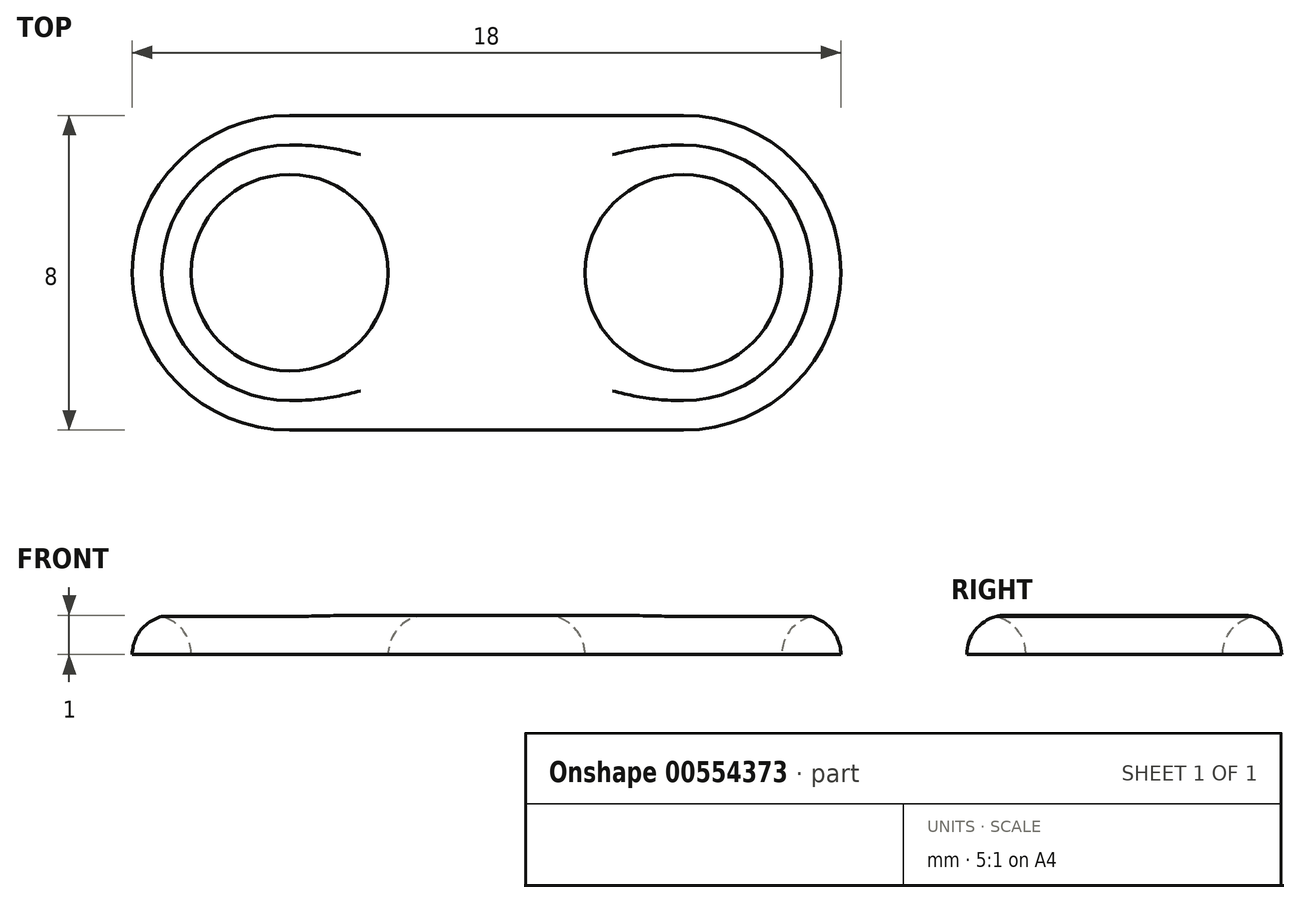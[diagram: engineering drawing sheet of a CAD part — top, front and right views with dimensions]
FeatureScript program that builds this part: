
annotation { "Feature Type Name" : "Feature", "Feature Type Description" : "" }
export const myFeature = defineFeature(function(context is Context, id is Id, definition is map)
    precondition{}
    {
        {
            var Q0;
            Q0=qCreatedBy(makeId("Top.planeOp"),FACE);
            var sketch = newSketch(context, id + "F0", { "sketchPlane" : qUnion([Q0])});
            skCircle(sketch, "E0", {"center": v(-5, 0) * mm, "radius": 2.5 * mm});
            skCircle(sketch, "E1", {"center": v(5, 0) * mm, "radius": 2.5 * mm});
            skArc(sketch, "E2", {"start": v(-5, 4) * mm, "mid": v(-9, 0) * mm, "end": v(-5, -4) * mm});
            skArc(sketch, "E3.MirrorCS", {"start": v(5, 4) * mm, "mid": v(9, 0) * mm, "end": v(5, -4) * mm});
            skLineSegment(sketch, "E4", {"start": v(-5, 4) * mm, "end": v(5, 4) * mm});
            skLineSegment(sketch, "E5", {"start": v(-5, -4) * mm, "end": v(5, -4) * mm});
            skSolve(sketch);
        }
        {
            var Q0;
            Q0 = qSketchRegion(id + "F0", true);
            extrude(context, id + "F1", {"entities" : qUnion([Q0]), "depth" : 1 * mm, "offsetDistance" : 25 * mm});
        }
        {
            var Q0;
            Q0=makeQuery(id+"F1.opExtrude","CAP_EDGE",EDGE,{"disambiguationData":[OSD([sQuery(id+"F0.wireOp",EDGE,"E2")])],"isStart":false});
            var Q1;
            Q1=makeQuery(id+"F1.opExtrude","CAP_EDGE",EDGE,{"disambiguationData":[OSD([sQuery(id+"F0.wireOp",EDGE,"E0")])],"isStart":false});
            var Q2;
            Q2=makeQuery(id+"F1.opExtrude","CAP_EDGE",EDGE,{"disambiguationData":[OSD([sQuery(id+"F0.wireOp",EDGE,"E1")])],"isStart":false});
            fillet(context, id + "F2", {"entities" : qUnion([Q0, Q1, Q2]), "radius" : 1 * mm, "tangentPropagation" : true, "allowEdgeOverflow" : false});
        }
    });
